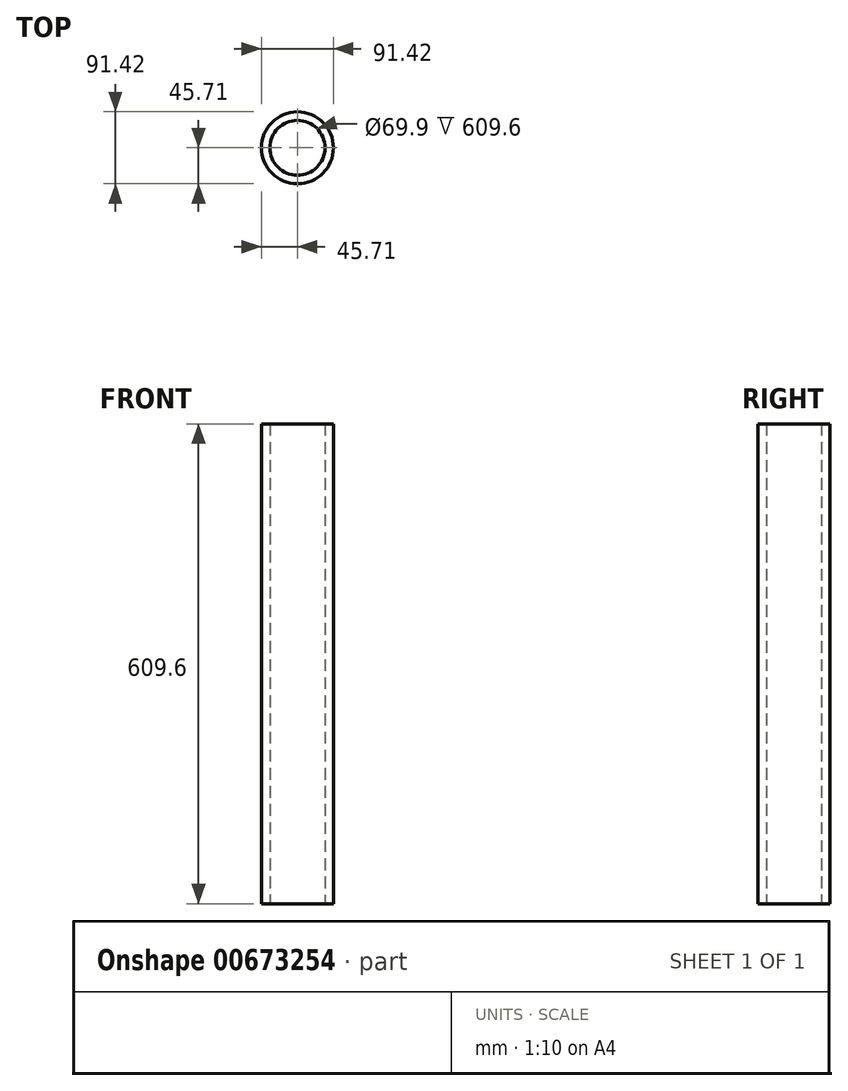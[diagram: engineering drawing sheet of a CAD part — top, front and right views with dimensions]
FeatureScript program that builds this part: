
annotation { "Feature Type Name" : "Feature", "Feature Type Description" : "" }
export const myFeature = defineFeature(function(context is Context, id is Id, definition is map)
    precondition{}
    {
        {
            var Q0;
            Q0=qCreatedBy(makeId("Top.planeOp"),FACE);
            var sketch = newSketch(context, id + "F0", { "sketchPlane" : qUnion([Q0])});
            skCircle(sketch, "E0", {"center": v(0, 0) * mm, "radius": 34.95 * mm});
            skCircle(sketch, "E1", {"center": v(0, 0) * mm, "radius": 45.71 * mm});
            skSolve(sketch);
        }
        {
            var Q0;
            Q0 = qSketchRegion(id + "F0", true);
            var Q1;
            Q1=makeQuery(id+"F0.imprint","IMPRINT",FACE,{"disambiguationData":[TD([[makeQuery(id+"F0.imprint","IMPRINT",EDGE,{"derivedFrom":sQuery(id+"F0.wireOp",EDGE,"E0")}),-1.0]])]});
            extrude(context, id + "F1", {"entities" : qUnion([Q0, Q1]), "depth" : 609.6 * mm, "offsetDistance" : 25.4 * mm});
        }
    });
